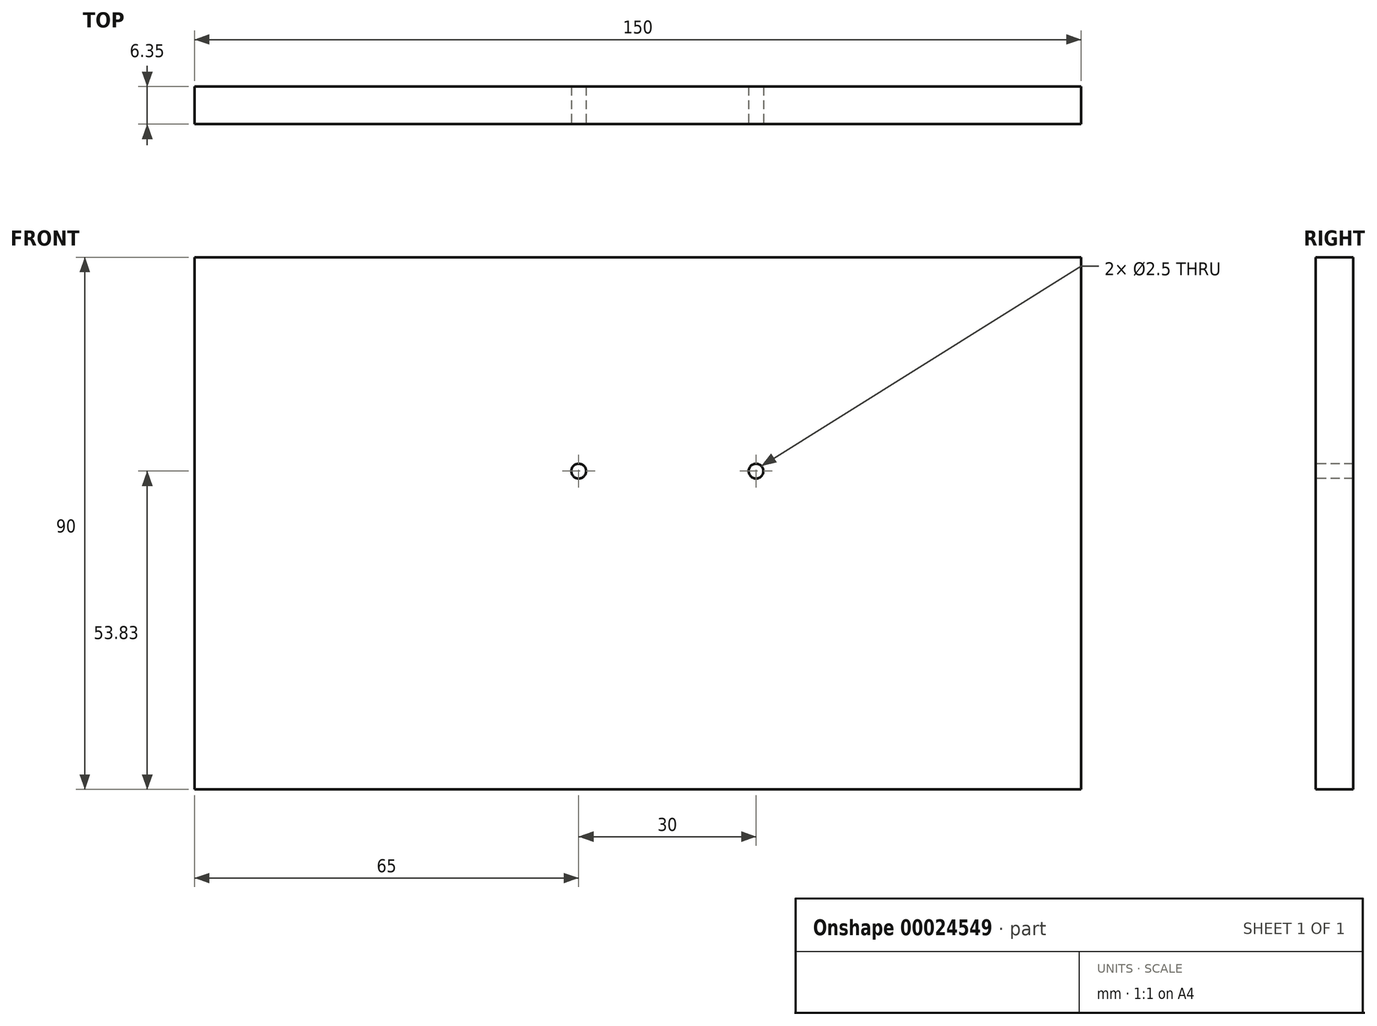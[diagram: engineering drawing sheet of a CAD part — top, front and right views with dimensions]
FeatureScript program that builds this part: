
annotation { "Feature Type Name" : "Feature", "Feature Type Description" : "" }
export const myFeature = defineFeature(function(context is Context, id is Id, definition is map)
    precondition{}
    {
        {
            var Q0;
            Q0=qCreatedBy(makeId("Front.planeOp"),FACE);
            var sketch = newSketch(context, id + "F0", { "sketchPlane" : qUnion([Q0])});
            skLineSegment(sketch, "E0.bottom", {"start": v(-65.48, 36.17) * mm, "end": v(84.52, 36.17) * mm});
            skLineSegment(sketch, "E0.top", {"start": v(-65.48, -53.83) * mm, "end": v(84.52, -53.83) * mm});
            skLineSegment(sketch, "E0.left", {"start": v(-65.48, 36.17) * mm, "end": v(-65.48, -53.83) * mm});
            skLineSegment(sketch, "E0.right", {"start": v(84.52, 36.17) * mm, "end": v(84.52, -53.83) * mm});
            skSolve(sketch);
        }
        {
            var Q0;
            Q0 = qSketchRegion(id + "F0", true);
            extrude(context, id + "F1", {"entities" : qUnion([Q0]), "depth" : 6.35 * mm});
        }
        {
            var Q0;
            Q0=makeQuery(id+"F1.opExtrude","CAP_FACE",FACE,{"disambiguationData":[OSD([sQuery(id+"F0.wireOp",EDGE,"E0.bottom"),sQuery(id+"F0.wireOp",EDGE,"E0.top"),sQuery(id+"F0.wireOp",EDGE,"E0.left"),sQuery(id+"F0.wireOp",EDGE,"E0.right")])],"isStart":false});
            var sketch = newSketch(context, id + "F2", { "sketchPlane" : qUnion([Q0])});
            skCircle(sketch, "E1", {"center": v(-0.48, 0) * mm, "radius": 1.25 * mm});
            skCircle(sketch, "E2", {"center": v(29.52, 0) * mm, "radius": 1.25 * mm});
            skSolve(sketch);
        }
        {
            var Q0;
            Q0=makeQuery(id+"F2.imprint","IMPRINT",FACE,{"disambiguationData":[TD([[makeQuery(id+"F2.imprint","IMPRINT",EDGE,{"derivedFrom":sQuery(id+"F2.wireOp",EDGE,"E1")}),1.0]])]});
            var Q1;
            Q1=makeQuery(id+"F2.imprint","IMPRINT",FACE,{"disambiguationData":[TD([[makeQuery(id+"F2.imprint","IMPRINT",EDGE,{"derivedFrom":sQuery(id+"F2.wireOp",EDGE,"E2")}),1.0]])]});
            extrude(context, id + "F3", {"entities" : qUnion([Q0, Q1]), "operationType" : NewBodyOperationType.REMOVE, "endBound" : BoundingType.THROUGH_ALL, "oppositeDirection" : true, "depth" : 25.4 * mm});
        }
    });
